# Revit family: Haworth_Comforto59_Chair_Side_Visitor_EU_PRELIMINARY
name_source: partatom
category: Furniture
units: mm (PartAtom-declared; Revit-internal decimal feet)

## family parameters
Always vertical = Yes
Cut with Voids When Loaded = No
OmniClass Number = 23.40.70.14.64.11
OmniClass Title = Office Furniture
Room Calculation Point = No
Shared = No
Work Plane-Based = No

## types (8) — shared parameters
Actual Depth = 65 cm
Actual Height = 97 cm
Actual Width = 69 cm
Arm Cap Finish = Haworth _ Polymer _ Undecided
Assembly Code = E2020200
Description = Haworth - Comforto 59 - Visitor Chair
Manufacturer = Haworth
Model = 59X0
Note = Verify Final Dim. w/ Haworth
Revision Number = 1
URL = https://www.haworth.com
URL - Product = https://www.haworth.com
Warranty = http://www.haworth.com

## per-type parameters (varying)
| type | Armless | Four Legs | Glide Finish | Mesh Back | Sled Base | Support Column | Upholstered Back | With Arms |
| With Arms - Upholstered Back - Four legs | No | Yes | Haworth _ Polymer _ Undecided | No | No | No | Yes | Yes |
| With Arms - Mesh Back - Sled Base | No | No | Haworth _ Polymer _ Undecided | Yes | Yes | No | No | Yes |
| Without Arms - Mesh Back - Sled Base | Yes | No | Haworth _ Polymer _ Undecided | Yes | Yes | Yes | No | No |
| With Arms - Mesh Back - Four Legs | No | Yes | Haworth _ Polymer _ Undecided | Yes | No | No | No | Yes |
| Without Arms - Mesh Back - Four Legs | Yes | Yes | Haworth _ Polymer _ Undecided | Yes | No | No | No | No |
| Without Arms - Upholstered Back - Four legs | Yes | Yes | Haworth _ Polymer _ Undecided | No | No | No | Yes | No |
| With Arms - Upholstered Back - Sled Base | No | No | Haworth _ Polymer _ Black | No | Yes | No | Yes | Yes |
| Without Arms - Upholstered Back - Sled Base | Yes | No | Haworth _ Polymer _ Black | No | Yes | Yes | Yes | No |

## geometry (parser evidence)
native form markers: Sweep x10
no freeform markers — native parametric forms only
